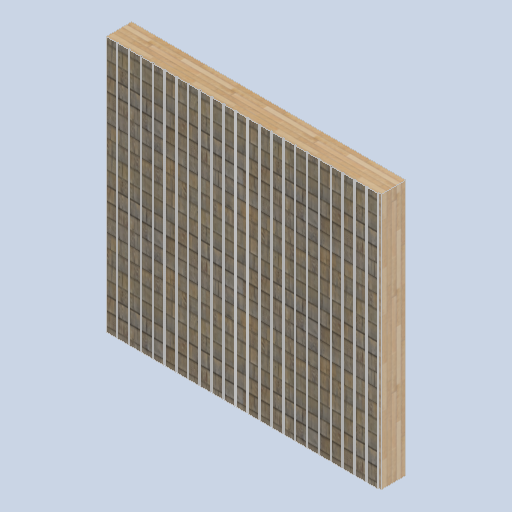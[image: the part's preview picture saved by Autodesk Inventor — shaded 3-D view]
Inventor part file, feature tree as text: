
AUTODESK INVENTOR PART (.ipt)
format: ipt  version: 2024.2 (Build 282272000, 272)  size: 593,408 bytes
history: native  units: mm
features: extrude x2, sketch x2
ambient origin geometry x8: Origin, YZ Plane, XZ Plane, XY Plane, X Axis, Y Axis, Z Axis, Center Point
bodies: Solid1 (feature_tree)
feature tree (4):
  extrude  "Extrusion1"  Depth=120.0mm
  extrude  "Extrusion2"  Depth=120.0mm
  sketch  "Sketch2"  dims[d0=300.0mm d1=0.0mm d2=120.0mm]
  sketch  "Sketch3"  dims[d3=90.0deg d4=120.0mm d5=120.0mm d6=120.0mm d7=120.0mm d8=120.0mm d9=120.0mm d10=120.0mm d11=120.0mm d12=120.0mm d13=120.0mm d14=120.0mm d15=120.0mm d16=120.0mm d17=120.0mm d18=120.0mm d19=120.0mm d20=120.0mm d21=120.0mm d22=120.0mm d23=120.0mm d24=120.0mm d25=120.0mm d26=0.0mm d27=0.0mm]
